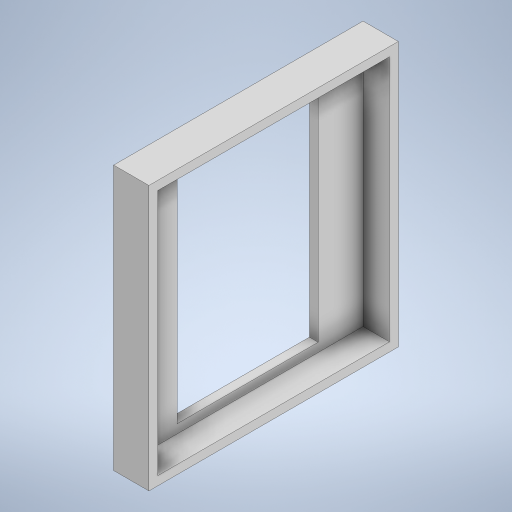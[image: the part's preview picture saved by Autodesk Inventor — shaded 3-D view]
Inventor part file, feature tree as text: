
AUTODESK INVENTOR PART (.ipt)
format: ipt  version: 2023 (Build 270158000, 158)  size: 241,664 bytes
history: native  units: in
note: dims shown in document units (in); Inventor stores cm internally (conversion verified against a paired STEP export)
features: extrude x2, sketch x2, shell x1
ambient origin geometry x8: Origin, YZ Plane, XZ Plane, XY Plane, X Axis, Y Axis, Z Axis, Center Point
bodies: Solid1 (feature_tree)
feature tree (5):
  extrude  "Extrusion1"  Depth=7.071in
  shell  "Shell1"  Thickness=1.0in
  extrude  "Extrusion2"  Depth=6.5in
  sketch  "Sketch1"  dims[d0=7.5in d1=7.071in d2=1.0in d3=0.0in]
  sketch  "Sketch2"  dims[d4=0.25in d5=6.5in d6=4.0in d7=0.25in d8=1.3in d9=0.0in d10=0.0in]
